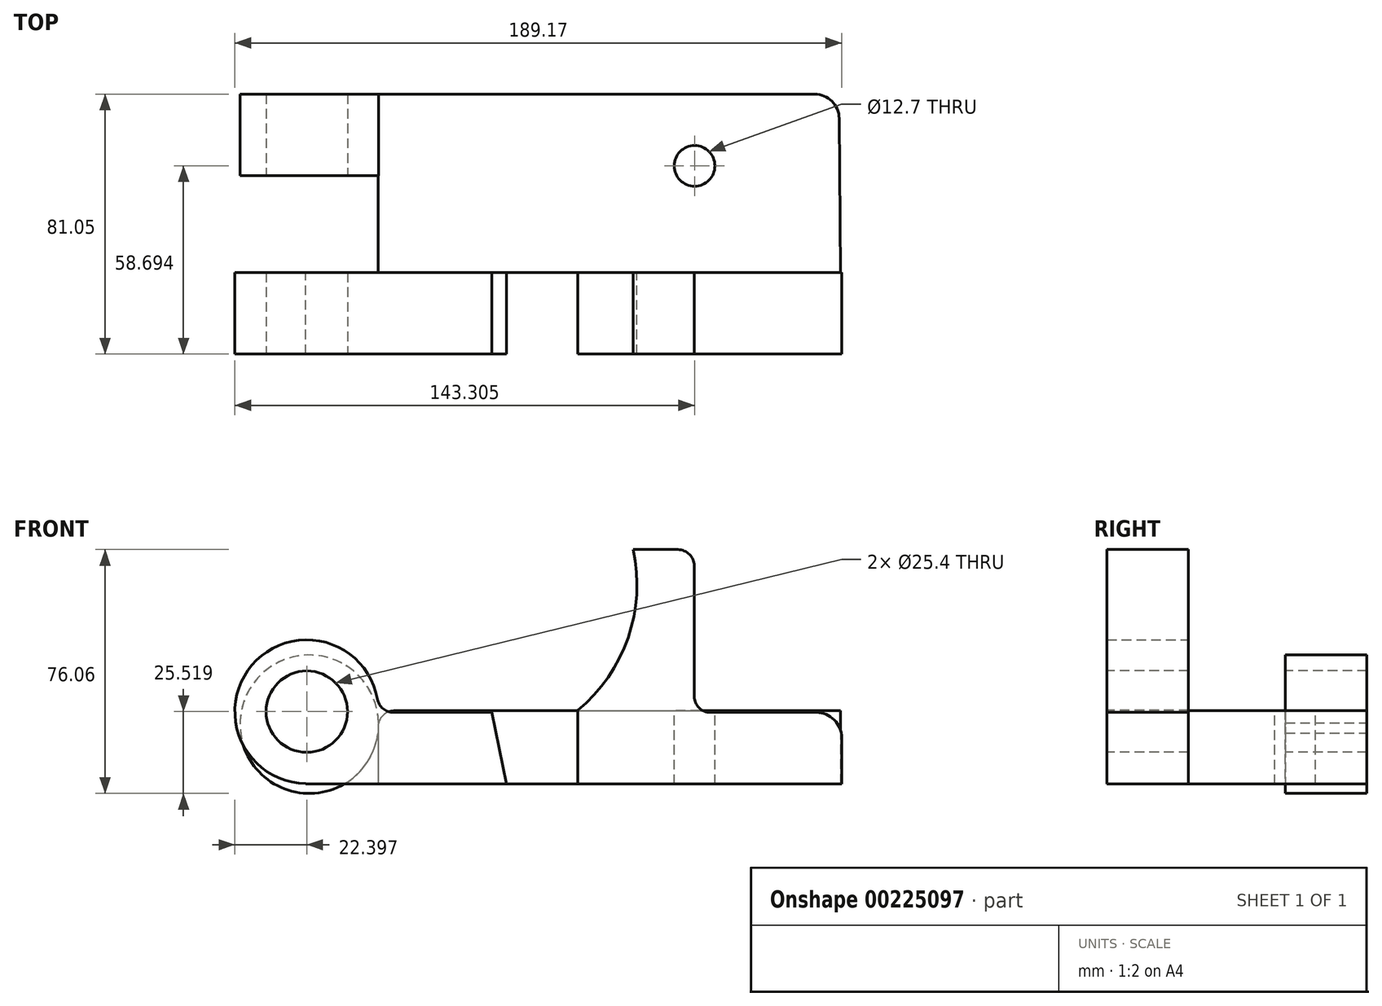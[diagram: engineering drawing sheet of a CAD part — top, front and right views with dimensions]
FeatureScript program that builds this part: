
annotation { "Feature Type Name" : "Feature", "Feature Type Description" : "" }
export const myFeature = defineFeature(function(context is Context, id is Id, definition is map)
    precondition{}
    {
        {
            var Q0;
            Q0=qCreatedBy(makeId("Front.planeOp"),FACE);
            var sketch = newSketch(context, id + "F0", { "sketchPlane" : qUnion([Q0])});
            skLineSegment(sketch, "E0", {"start": v(104.55, 0) * mm, "end": v(-62.57, 0) * mm});
            skLineSegment(sketch, "E1", {"start": v(104.55, 0) * mm, "end": v(104.55, 14.48) * mm});
            skLineSegment(sketch, "E2", {"start": v(96.67, 22.35) * mm, "end": v(58.57, 22.35) * mm});
            skPoint(sketch, "E3.visualSharp", {"position": v(104.55, 22.35) * mm});
            skArc(sketch, "E3.filletArc", {"start": v(104.55, 14.48) * mm, "mid": v(102.24, 20.05) * mm, "end": v(96.67, 22.35) * mm});
            skLineSegment(sketch, "E4", {"start": v(58.57, 22.35) * mm, "end": v(58.57, 73.15) * mm});
            skLineSegment(sketch, "E5", {"start": v(58.57, 73.15) * mm, "end": v(39.52, 73.15) * mm});
            skLineSegment(sketch, "E6", {"start": v(-62.57, 22.35) * mm, "end": v(21.47, 22.35) * mm});
            skArc(sketch, "E7", {"start": v(21.47, 22.35) * mm, "mid": v(37.8, 45.16) * mm, "end": v(39.52, 73.15) * mm});
            skLineSegment(sketch, "E8", {"start": v(-62.57, 0) * mm, "end": v(-62.57, 22.35) * mm});
            skSolve(sketch);
        }
        {
            var Q0;
            Q0 = qSketchRegion(id + "F0", true);
            extrude(context, id + "F1", {"entities" : qUnion([Q0]), "depth" : 25.4 * mm});
        }
        {
            var Q0;
            Q0=qCreatedBy(makeId("Front.planeOp"),FACE);
            var sketch = newSketch(context, id + "F2", { "sketchPlane" : qUnion([Q0])});
            skCircle(sketch, "E9", {"center": v(-62.22, 22.6) * mm, "radius": 22.4 * mm});
            skSolve(sketch);
        }
        {
            var Q0;
            Q0 = qSketchRegion(id + "F2", true);
            extrude(context, id + "F3", {"entities" : qUnion([Q0]), "operationType" : NewBodyOperationType.ADD, "depth" : 25.4 * mm});
        }
        {
            var Q0;
            Q0=qCreatedBy(makeId("Top.planeOp"),FACE);
            var sketch = newSketch(context, id + "F4", { "sketchPlane" : qUnion([Q0])});
            skLineSegment(sketch, "E10", {"start": v(-40, 0) * mm, "end": v(-40, 55.65) * mm});
            skLineSegment(sketch, "E11", {"start": v(-40, 55.65) * mm, "end": v(96.17, 55.65) * mm});
            skLineSegment(sketch, "E12", {"start": v(104.15, 0) * mm, "end": v(103.79, 48.08) * mm});
            skPoint(sketch, "E13.visualSharp", {"position": v(103.73, 55.65) * mm});
            skArc(sketch, "E13.filletArc", {"start": v(103.79, 48.08) * mm, "mid": v(101.54, 53.43) * mm, "end": v(96.17, 55.65) * mm});
            skLineSegment(sketch, "E14", {"start": v(-40, 0) * mm, "end": v(104.15, 0) * mm});
            skSolve(sketch);
        }
        {
            var Q0;
            Q0 = qSketchRegion(id + "F4", true);
            extrude(context, id + "F5", {"entities" : qUnion([Q0]), "operationType" : NewBodyOperationType.ADD, "depth" : 22.86 * mm});
        }
        {
            var Q0;
            Q0=makeQuery(id+"F5.opExtrude","CAP_FACE",FACE,{"disambiguationData":[OSD([sQuery(id+"F4.wireOp",EDGE,"E10"),sQuery(id+"F4.wireOp",EDGE,"E11"),sQuery(id+"F4.wireOp",EDGE,"E12"),sQuery(id+"F4.wireOp",EDGE,"E13.filletArc"),sQuery(id+"F4.wireOp",EDGE,"E14")])],"isStart":false});
            var sketch = newSketch(context, id + "F6", { "sketchPlane" : qUnion([Q0])});
            skCircle(sketch, "E15", {"center": v(58.68, 33.3) * mm, "radius": 6.35 * mm});
            skLineSegment(sketch, "E16", {"start": v(22.1, 0) * mm, "end": v(22.1, 14.47) * mm});
            skLineSegment(sketch, "E17", {"start": v(22.1, 14.47) * mm, "end": v(2.17, 14.47) * mm});
            skLineSegment(sketch, "E18", {"start": v(2.17, 14.47) * mm, "end": v(0, 0) * mm});
            skLineSegment(sketch, "E19", {"start": v(0, 0) * mm, "end": v(22.1, 0) * mm});
            skSolve(sketch);
        }
        {
            var Q0;
            Q0=makeQuery(id+"F6.imprint","IMPRINT",FACE,{"disambiguationData":[TD([[makeQuery(id+"F6.imprint","IMPRINT",EDGE,{"derivedFrom":sQuery(id+"F6.wireOp",EDGE,"E15")}),1.0]])]});
            extrude(context, id + "F7", {"entities" : qUnion([Q0]), "operationType" : NewBodyOperationType.REMOVE, "endBound" : BoundingType.THROUGH_ALL, "oppositeDirection" : true, "depth" : 25.4 * mm});
        }
        {
            var Q0;
            Q0=makeQuery(id+"F3.boolean.opBoolean","MERGE",FACE,{"derivedFrom":[makeQuery(id+"F1.opExtrude","CAP_FACE",FACE,{"disambiguationData":[OSD([sQuery(id+"F0.wireOp",EDGE,"E0"),sQuery(id+"F0.wireOp",EDGE,"E1"),sQuery(id+"F0.wireOp",EDGE,"E2"),sQuery(id+"F0.wireOp",EDGE,"E3.filletArc"),sQuery(id+"F0.wireOp",EDGE,"E4"),sQuery(id+"F0.wireOp",EDGE,"E5"),sQuery(id+"F0.wireOp",EDGE,"E6"),sQuery(id+"F0.wireOp",EDGE,"E7"),sQuery(id+"F0.wireOp",EDGE,"E8")])],"isStart":false}),makeQuery(id+"F3.opExtrude","CAP_FACE",FACE,{"disambiguationData":[OSD([sQuery(id+"F2.wireOp",EDGE,"E9")])],"isStart":false})]});
            var sketch = newSketch(context, id + "F8", { "sketchPlane" : qUnion([Q0])});
            skLineSegment(sketch, "E20", {"start": v(22.28, 23) * mm, "end": v(22.28, 0) * mm});
            skPoint(sketch, "E20.endSnap0", {"position": v(20.99, 0) * mm});
            skLineSegment(sketch, "E21", {"start": v(22.28, 0) * mm, "end": v(0, 0) * mm});
            skLineSegment(sketch, "E22", {"start": v(0, 0) * mm, "end": v(-4.49, 22.35) * mm});
            skLineSegment(sketch, "E23", {"start": v(-4.49, 22.35) * mm, "end": v(21.47, 22.35) * mm});
            skSolve(sketch);
        }
        {
            var Q0;
            {var subQ1=sQuery(id+"F8.wireOp",EDGE,"E20");Q0=makeQuery(id+"F8.imprint","IMPRINT",FACE,{"disambiguationData":[TD([[makeQuery(id+"F8.imprint","IMPRINT",EDGE,{"derivedFrom":subQ1}),-1.0]])]});}
            extrude(context, id + "F9", {"entities" : qUnion([Q0]), "operationType" : NewBodyOperationType.REMOVE, "oppositeDirection" : true, "depth" : 25.4 * mm});
        }
        {
            var Q0;
            Q0=makeQuery(id+"F1.opExtrude","SWEPT_EDGE",EDGE,{"disambiguationData":[OSD([sQuery(id+"F0.wireOp",EDGE,"E4"),sQuery(id+"F0.wireOp",EDGE,"E5")])]});
            var Q1;
            Q1=makeQuery(id+"F1.opExtrude","SWEPT_EDGE",EDGE,{"disambiguationData":[OSD([sQuery(id+"F0.wireOp",EDGE,"E2"),sQuery(id+"F0.wireOp",EDGE,"E4")])]});
            var Q2;
            Q2=makeQuery(id+"F3.boolean.opBoolean","INTERSECT",EDGE,{"derivedFrom":[makeQuery(id+"F1.opExtrude","SWEPT_FACE",FACE,{"disambiguationData":[OSD([sQuery(id+"F0.wireOp",EDGE,"E6")])]}),makeQuery(id+"F3.opExtrude","SWEPT_FACE",FACE,{"disambiguationData":[OSD([sQuery(id+"F2.wireOp",EDGE,"E9")])]})]});
            fillet(context, id + "F10", {"entities" : qUnion([Q0, Q1, Q2]), "radius" : 5.08 * mm, "tangentPropagation" : true, "allowEdgeOverflow" : false});
        }
        {
            var Q0;
            Q0=makeQuery(id+"F5.opExtrude","SWEPT_FACE",FACE,{"disambiguationData":[OSD([sQuery(id+"F4.wireOp",EDGE,"E11")])]});
            var sketch = newSketch(context, id + "F11", { "sketchPlane" : qUnion([Q0])});
            skCircle(sketch, "E24", {"center": v(61.42, 18.68) * mm, "radius": 21.59 * mm});
            skSolve(sketch);
        }
        {
            var Q0;
            Q0 = qSketchRegion(id + "F11", true);
            extrude(context, id + "F12", {"entities" : qUnion([Q0]), "operationType" : NewBodyOperationType.ADD, "oppositeDirection" : true, "depth" : 25.4 * mm});
        }
        {
            var Q0;
            Q0=makeQuery(id+"F5.opExtrude","CAP_EDGE",EDGE,{"disambiguationData":[OSD([sQuery(id+"F4.wireOp",EDGE,"E10")])],"isStart":false});
            fillet(context, id + "F13", {"entities" : qUnion([Q0]), "radius" : 5.08 * mm, "tangentPropagation" : true, "allowEdgeOverflow" : false});
        }
        {
            var Q0;
            {var subQ0=sQuery(id+"F0.wireOp",EDGE,"E8");var subQ1=sQuery(id+"F0.wireOp",EDGE,"E6");var subQ2=sQuery(id+"F2.wireOp",EDGE,"E9");var subQ3=sQuery(id+"F0.wireOp",EDGE,"E0");Q0=makeQuery(id+"F9.boolean.opBoolean","SPLIT",FACE,{"disambiguationData":[TD([makeQuery(id+"F1.opExtrude","SWEPT_FACE",FACE,{"disambiguationData":[OSD([subQ1])]})])],"derivedFrom":makeQuery(id+"F3.boolean.opBoolean","MERGE",FACE,{"derivedFrom":[makeQuery(id+"F1.opExtrude","CAP_FACE",FACE,{"disambiguationData":[OSD([subQ3,sQuery(id+"F0.wireOp",EDGE,"E1"),sQuery(id+"F0.wireOp",EDGE,"E2"),sQuery(id+"F0.wireOp",EDGE,"E3.filletArc"),sQuery(id+"F0.wireOp",EDGE,"E4"),sQuery(id+"F0.wireOp",EDGE,"E5"),subQ1,sQuery(id+"F0.wireOp",EDGE,"E7"),subQ0])],"isStart":false}),makeQuery(id+"F3.opExtrude","CAP_FACE",FACE,{"disambiguationData":[OSD([subQ2])],"isStart":false})]})});}
            var sketch = newSketch(context, id + "F14", { "sketchPlane" : qUnion([Q0])});
            skCircle(sketch, "E25", {"center": v(-62.22, 22.6) * mm, "radius": 12.7 * mm});
            skSolve(sketch);
        }
        {
            var Q0;
            Q0 = qSketchRegion(id + "F14", true);
            extrude(context, id + "F15", {"entities" : qUnion([Q0]), "operationType" : NewBodyOperationType.REMOVE, "endBound" : BoundingType.THROUGH_ALL, "oppositeDirection" : true, "depth" : 25.4 * mm});
        }
    });
